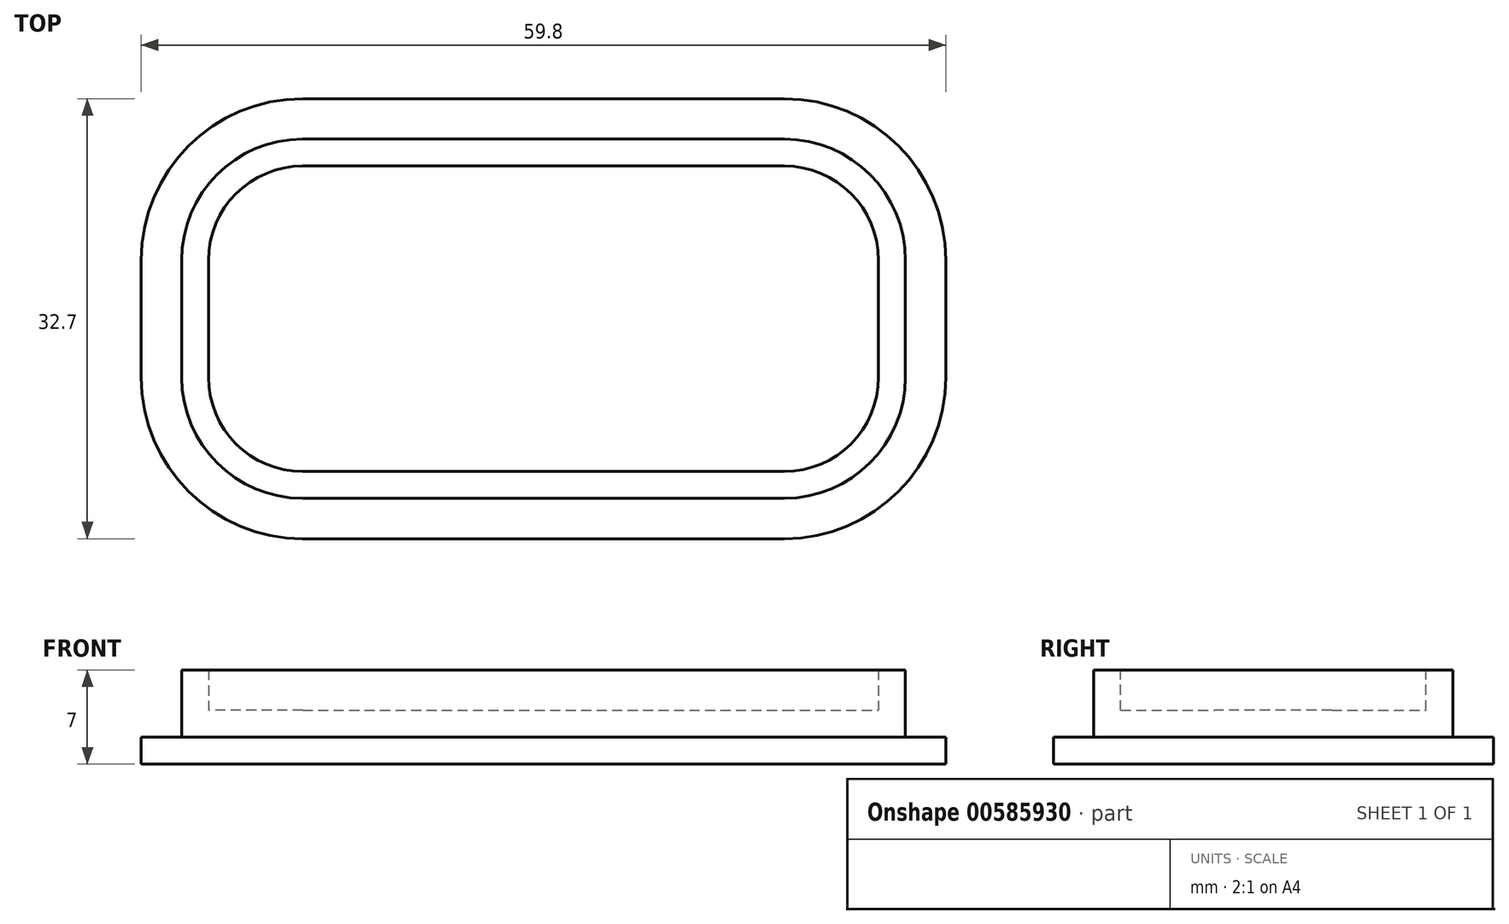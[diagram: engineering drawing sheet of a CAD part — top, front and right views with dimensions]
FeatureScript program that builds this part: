
annotation { "Feature Type Name" : "Feature", "Feature Type Description" : "" }
export const myFeature = defineFeature(function(context is Context, id is Id, definition is map)
    precondition{}
    {
        {
            var Q0;
            Q0=qCreatedBy(makeId("Top.planeOp"),FACE);
            var sketch = newSketch(context, id + "F0", { "sketchPlane" : qUnion([Q0])});
            skLineSegment(sketch, "E0.bottom", {"start": v(-36.37, 16.14) * mm, "end": v(17.43, 16.14) * mm});
            skLineSegment(sketch, "E0.top", {"start": v(-36.37, -10.56) * mm, "end": v(17.43, -10.56) * mm});
            skLineSegment(sketch, "E0.left", {"start": v(-36.37, 16.14) * mm, "end": v(-36.37, -10.56) * mm});
            skLineSegment(sketch, "E0.right", {"start": v(17.43, 16.14) * mm, "end": v(17.43, -10.56) * mm});
            skSolve(sketch);
        }
        {
            var Q0;
            Q0=makeQuery(id+"F0.imprint","IMPRINT",FACE,{"disambiguationData":[TD([[makeQuery(id+"F0.imprint","IMPRINT",EDGE,{"derivedFrom":sQuery(id+"F0.wireOp",EDGE,"E0.bottom")}),-1.0]])]});
            extrude(context, id + "F1", {"entities" : qUnion([Q0]), "depth" : 5 * mm, "offsetDistance" : 25 * mm});
        }
        {
            var Q0;
            Q0=makeQuery(id+"F1.opExtrude","SWEPT_EDGE",EDGE,{"disambiguationData":[OSD([sQuery(id+"F0.wireOp",EDGE,"E0.bottom"),sQuery(id+"F0.wireOp",EDGE,"E0.left")])]});
            var Q1;
            Q1=makeQuery(id+"F1.opExtrude","SWEPT_EDGE",EDGE,{"disambiguationData":[OSD([sQuery(id+"F0.wireOp",EDGE,"E0.bottom"),sQuery(id+"F0.wireOp",EDGE,"E0.right")])]});
            var Q2;
            Q2=makeQuery(id+"F1.opExtrude","SWEPT_EDGE",EDGE,{"disambiguationData":[OSD([sQuery(id+"F0.wireOp",EDGE,"E0.top"),sQuery(id+"F0.wireOp",EDGE,"E0.right")])]});
            var Q3;
            Q3=makeQuery(id+"F1.opExtrude","SWEPT_EDGE",EDGE,{"disambiguationData":[OSD([sQuery(id+"F0.wireOp",EDGE,"E0.top"),sQuery(id+"F0.wireOp",EDGE,"E0.left")])]});
            fillet(context, id + "F2", {"entities" : qUnion([Q0, Q1, Q2, Q3]), "radius" : 9 * mm, "tangentPropagation" : true, "allowEdgeOverflow" : false});
        }
        {
            var Q0;
            Q0=makeQuery(id+"F1.opExtrude","CAP_FACE",FACE,{"disambiguationData":[OSD([sQuery(id+"F0.wireOp",EDGE,"E0.bottom"),sQuery(id+"F0.wireOp",EDGE,"E0.top"),sQuery(id+"F0.wireOp",EDGE,"E0.left"),sQuery(id+"F0.wireOp",EDGE,"E0.right")])],"isStart":false});
            shell(context, id + "F3", {"entities" : qUnion([Q0]), "thickness" : 2 * mm});
        }
        {
            var Q0;
            Q0=makeQuery(id+"F1.opExtrude","CAP_FACE",FACE,{"disambiguationData":[OSD([sQuery(id+"F0.wireOp",EDGE,"E0.bottom"),sQuery(id+"F0.wireOp",EDGE,"E0.top"),sQuery(id+"F0.wireOp",EDGE,"E0.left"),sQuery(id+"F0.wireOp",EDGE,"E0.right")])],"isStart":true});
            var sketch = newSketch(context, id + "F4", { "sketchPlane" : qUnion([Q0])});
            skArc(sketch, "E1.0", {"start": v(20.43, 1.56) * mm, "mid": v(16.92, 10.04) * mm, "end": v(8.43, 13.56) * mm});
            skLineSegment(sketch, "E1.1", {"start": v(20.43, -7.14) * mm, "end": v(20.43, 1.56) * mm});
            skLineSegment(sketch, "E1.2", {"start": v(8.43, 13.56) * mm, "end": v(-27.37, 13.56) * mm});
            skArc(sketch, "E1.3", {"start": v(8.43, -19.14) * mm, "mid": v(16.92, -15.63) * mm, "end": v(20.43, -7.14) * mm});
            skArc(sketch, "E1.4", {"start": v(-27.37, 13.56) * mm, "mid": v(-35.85, 10.04) * mm, "end": v(-39.37, 1.56) * mm});
            skLineSegment(sketch, "E1.5", {"start": v(-39.37, 1.56) * mm, "end": v(-39.37, -7.14) * mm});
            skArc(sketch, "E1.6", {"start": v(-39.37, -7.14) * mm, "mid": v(-35.85, -15.63) * mm, "end": v(-27.37, -19.14) * mm});
            skLineSegment(sketch, "E1.7", {"start": v(-27.37, -19.14) * mm, "end": v(8.43, -19.14) * mm});
            skSolve(sketch);
        }
        {
            var Q0;
            Q0=makeQuery(id+"F4.imprint","IMPRINT",FACE,{"disambiguationData":[TD([[makeQuery(id+"F4.imprint","IMPRINT",EDGE,{"derivedFrom":sQuery(id+"F4.wireOp",EDGE,"E1.0")}),1.0]])]});
            var Q1;
            {var subQ3=sQuery(id+"F0.wireOp",EDGE,"E0.bottom");Q1=makeQuery(id+"F4.imprint","IMPRINT",FACE,{"disambiguationData":[TD([[makeQuery(id+"F4.imprint","IMPRINT",EDGE,{"derivedFrom":makeQuery(id+"F1.opExtrude","CAP_EDGE",EDGE,{"disambiguationData":[OSD([subQ3])],"isStart":true})}),1.0]])]});}
            extrude(context, id + "F5", {"entities" : qUnion([Q0, Q1]), "operationType" : NewBodyOperationType.ADD, "depth" : 2 * mm, "offsetDistance" : 25 * mm});
        }
    });
